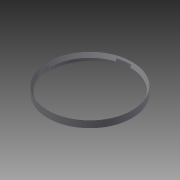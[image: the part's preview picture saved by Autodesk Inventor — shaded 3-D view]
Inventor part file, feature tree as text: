
AUTODESK INVENTOR PART (.ipt)
format: ipt  version: 2014 (Build 180170000, 170)  size: 109,056 bytes
history: native  units: in
note: dims shown in document units (in); Inventor stores cm internally (conversion verified against a paired STEP export)
features: sketch x3, revolve x1, extrude x1
ambient origin geometry x8: Origin, YZ Plane, XZ Plane, XY Plane, X Axis, Y Axis, Z Axis, Center Point
bodies: Solid1 (feature_tree)
feature tree (5):
  sketch  "Sketch1"  dims[d0=3.75in d1=3.584in]
  revolve  "Revolution1"  [1 undecoded]
  extrude  "Extrusion1"  Depth=0.1237in
  sketch  "Sketch2"  dims[d4=90.0deg d5=0.1237in d6=0.7421in d7=1.1132in d8=0.4947in]
  sketch  "Sketch3"  dims[d9=1.0in d10=0.0in]
note: 1 required parameter value undecoded (feature->parameter linkage not recoverable at this tier; creation-order binding heuristic only, values carry confidence <= 0.55)
